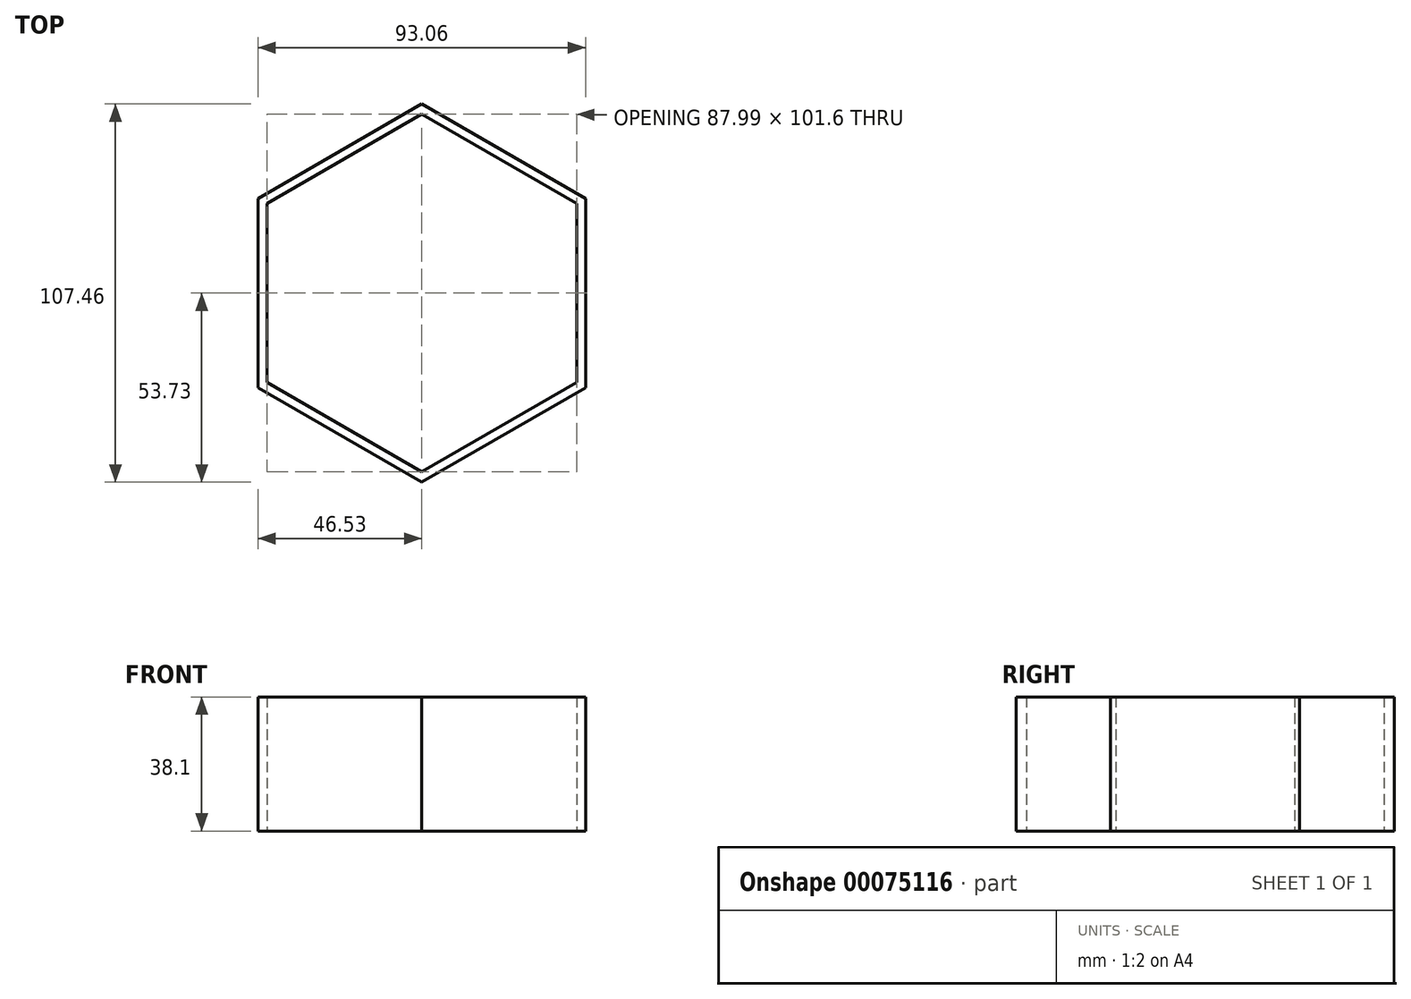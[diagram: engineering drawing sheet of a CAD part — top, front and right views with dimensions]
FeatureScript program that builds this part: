
annotation { "Feature Type Name" : "Feature", "Feature Type Description" : "" }
export const myFeature = defineFeature(function(context is Context, id is Id, definition is map)
    precondition{}
    {
        {
            var Q0;
            Q0=qCreatedBy(makeId("Top.planeOp"),FACE);
            var sketch = newSketch(context, id + "F0", { "sketchPlane" : qUnion([Q0])});
            skCircle(sketch, "E0.cCircle", {"center": v(0, 0) * mm, "radius": 44 * mm, "construction": true});
            skLineSegment(sketch, "E0.0", {"start": v(44, 25.4) * mm, "end": v(44, -25.4) * mm});
            skLineSegment(sketch, "E0.1", {"start": v(44, -25.4) * mm, "end": v(0, -50.8) * mm});
            skLineSegment(sketch, "E0.2", {"start": v(0, -50.8) * mm, "end": v(-44, -25.4) * mm});
            skLineSegment(sketch, "E0.3", {"start": v(-44, -25.4) * mm, "end": v(-44, 25.4) * mm});
            skLineSegment(sketch, "E0.4", {"start": v(-44, 25.4) * mm, "end": v(0, 50.8) * mm});
            skLineSegment(sketch, "E0.5", {"start": v(0, 50.8) * mm, "end": v(44, 25.4) * mm});
            skPoint(sketch, "E0.0.midPoint", {"position": v(44, 0) * mm});
            skLineSegment(sketch, "E1.0", {"start": v(-46.53, 26.87) * mm, "end": v(0, 53.73) * mm});
            skLineSegment(sketch, "E1.1", {"start": v(46.53, 26.87) * mm, "end": v(46.53, -26.87) * mm});
            skLineSegment(sketch, "E1.2", {"start": v(46.53, -26.87) * mm, "end": v(0, -53.73) * mm});
            skLineSegment(sketch, "E1.3", {"start": v(0, 53.73) * mm, "end": v(46.53, 26.87) * mm});
            skLineSegment(sketch, "E1.4", {"start": v(0, -53.73) * mm, "end": v(-46.53, -26.87) * mm});
            skLineSegment(sketch, "E1.5", {"start": v(-46.53, -26.87) * mm, "end": v(-46.53, 26.87) * mm});
            skSolve(sketch);
        }
        {
            var Q0;
            Q0 = qSketchRegion(id + "F0", true);
            extrude(context, id + "F1", {"entities" : qUnion([Q0]), "depth" : 38.1 * mm});
        }
    });
